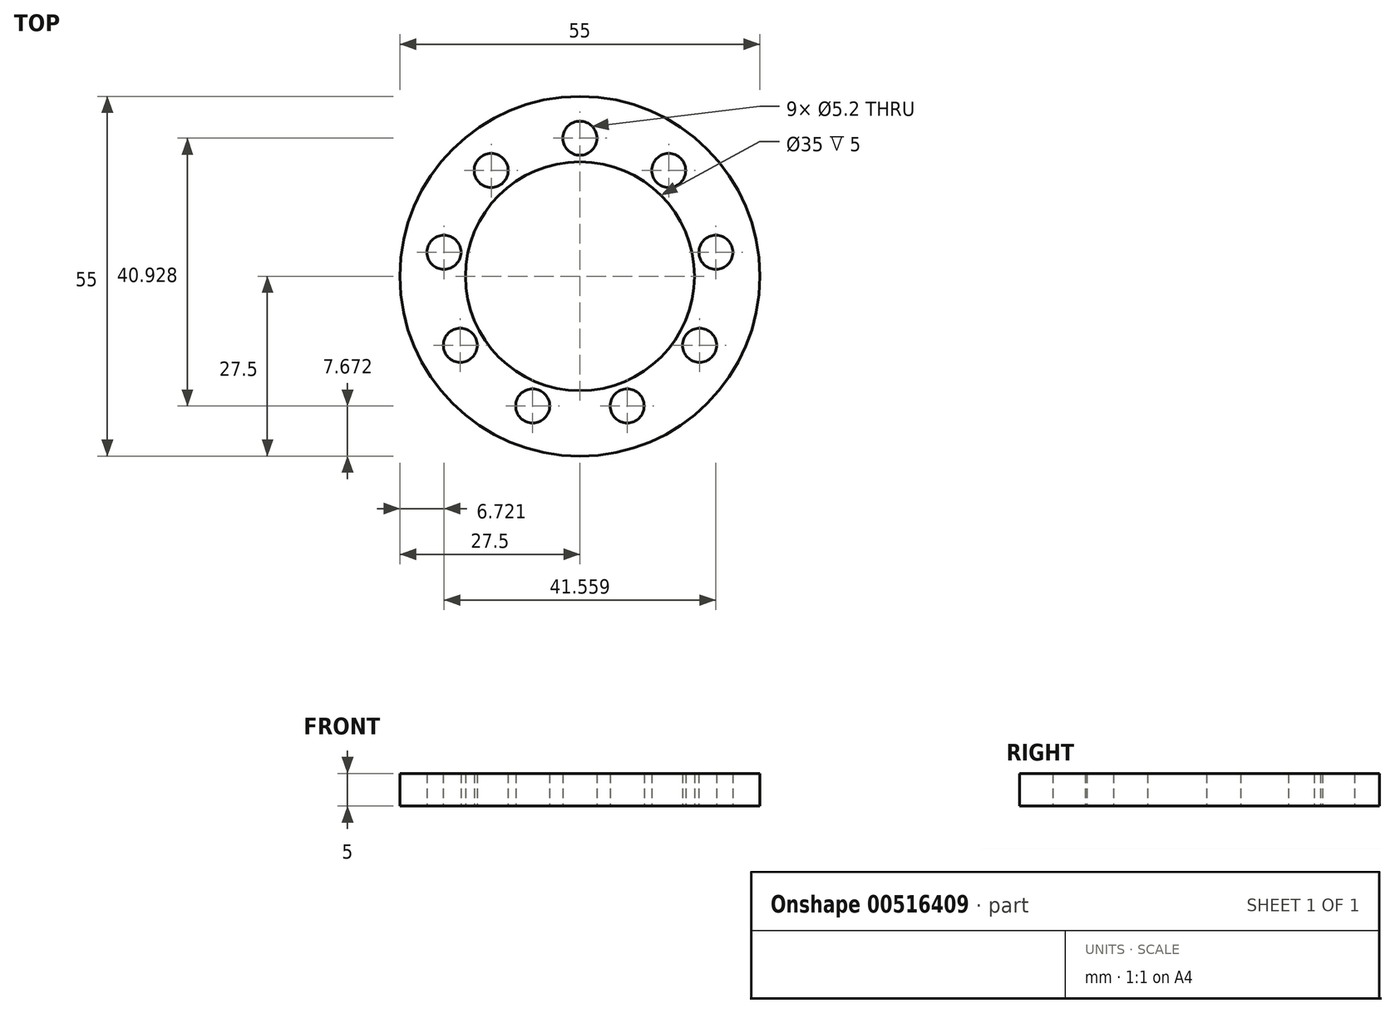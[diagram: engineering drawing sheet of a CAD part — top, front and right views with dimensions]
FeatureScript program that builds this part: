
annotation { "Feature Type Name" : "Feature", "Feature Type Description" : "" }
export const myFeature = defineFeature(function(context is Context, id is Id, definition is map)
    precondition{}
    {
        {
            var Q0;
            Q0=qCreatedBy(makeId("Top.planeOp"),FACE);
            var sketch = newSketch(context, id + "F0", { "sketchPlane" : qUnion([Q0])});
            skCircle(sketch, "E0", {"center": v(0, 0) * mm, "radius": 17.5 * mm});
            skCircle(sketch, "E1", {"center": v(0, 21.1) * mm, "radius": 2.6 * mm});
            skCircle(sketch, "E2", {"center": v(0, 0) * mm, "radius": 27.5 * mm});
            skCircle(sketch, "E3.1.0", {"center": v(-13.56, 16.16) * mm, "radius": 2.6 * mm});
            skCircle(sketch, "E3.2.0", {"center": v(-20.78, 3.66) * mm, "radius": 2.6 * mm});
            skCircle(sketch, "E3.3.0", {"center": v(-18.27, -10.55) * mm, "radius": 2.6 * mm});
            skCircle(sketch, "E3.4.0", {"center": v(-7.22, -19.83) * mm, "radius": 2.6 * mm});
            skCircle(sketch, "E3.5.0", {"center": v(7.22, -19.83) * mm, "radius": 2.6 * mm});
            skCircle(sketch, "E3.6.0", {"center": v(18.27, -10.55) * mm, "radius": 2.6 * mm});
            skCircle(sketch, "E3.7.0", {"center": v(20.78, 3.66) * mm, "radius": 2.6 * mm});
            skCircle(sketch, "E3.8.0", {"center": v(13.56, 16.16) * mm, "radius": 2.6 * mm});
            skSolve(sketch);
        }
        {
            var Q0;
            Q0 = qSketchRegion(id + "F0", true);
            extrude(context, id + "F1", {"entities" : qUnion([Q0]), "depth" : 5 * mm, "offsetDistance" : 25 * mm});
        }
    });
